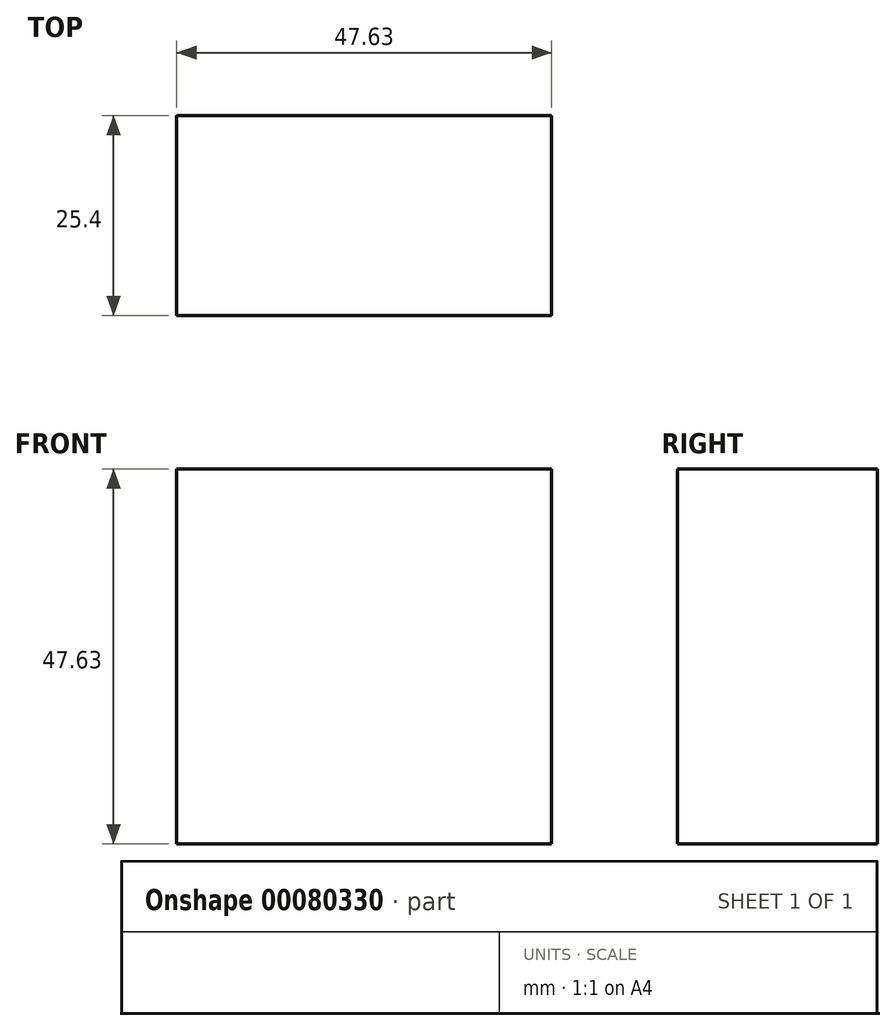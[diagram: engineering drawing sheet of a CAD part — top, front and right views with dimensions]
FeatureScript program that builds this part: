
annotation { "Feature Type Name" : "Feature", "Feature Type Description" : "" }
export const myFeature = defineFeature(function(context is Context, id is Id, definition is map)
    precondition{}
    {
        {
            var Q0;
            Q0=qCreatedBy(makeId("Front.planeOp"),FACE);
            var sketch = newSketch(context, id + "F0", { "sketchPlane" : qUnion([Q0])});
            skLineSegment(sketch, "E0.bottom", {"start": v(-25.1, 31.3) * mm, "end": v(22.53, 31.3) * mm});
            skLineSegment(sketch, "E0.top", {"start": v(-25.1, -16.32) * mm, "end": v(22.53, -16.32) * mm});
            skLineSegment(sketch, "E0.left", {"start": v(-25.1, 31.3) * mm, "end": v(-25.1, -16.32) * mm});
            skLineSegment(sketch, "E0.right", {"start": v(22.53, 31.3) * mm, "end": v(22.53, -16.32) * mm});
            skSolve(sketch);
        }
        {
            var Q0;
            Q0=makeQuery(id+"F0.imprint","IMPRINT",FACE,{"disambiguationData":[TD([[makeQuery(id+"F0.imprint","IMPRINT",EDGE,{"derivedFrom":sQuery(id+"F0.wireOp",EDGE,"E0.bottom")}),-1.0]])]});
            extrude(context, id + "F1", {"entities" : qUnion([Q0]), "depth" : 25.4 * mm});
        }
    });
